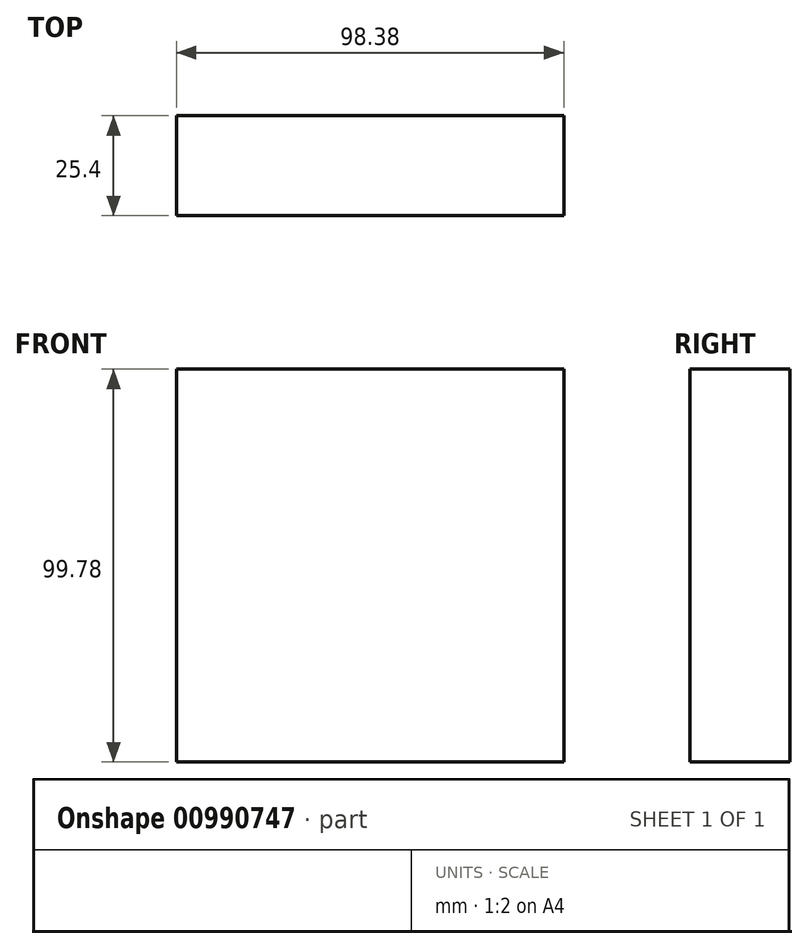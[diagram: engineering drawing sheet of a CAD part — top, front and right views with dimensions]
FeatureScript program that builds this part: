
annotation { "Feature Type Name" : "Feature", "Feature Type Description" : "" }
export const myFeature = defineFeature(function(context is Context, id is Id, definition is map)
    precondition{}
    {
        {
            var Q0;
            Q0=qCreatedBy(makeId("Front.planeOp"),FACE);
            var sketch = newSketch(context, id + "F0", { "sketchPlane" : qUnion([Q0])});
            skLineSegment(sketch, "E0.bottom", {"start": v(49.2, 49.89) * mm, "end": v(-49.2, 49.89) * mm});
            skLineSegment(sketch, "E0.top", {"start": v(49.2, -49.89) * mm, "end": v(-49.2, -49.89) * mm});
            skLineSegment(sketch, "E0.left", {"start": v(49.2, 49.89) * mm, "end": v(49.2, -49.89) * mm});
            skLineSegment(sketch, "E0.right", {"start": v(-49.2, 49.89) * mm, "end": v(-49.2, -49.89) * mm});
            skPoint(sketch, "E0.middle", {"position": v(0, 0) * mm});
            skSolve(sketch);
        }
        {
            var Q0;
            Q0=makeQuery(id+"F0.imprint","IMPRINT",FACE,{"disambiguationData":[TD([[makeQuery(id+"F0.imprint","IMPRINT",EDGE,{"derivedFrom":sQuery(id+"F0.wireOp",EDGE,"E0.bottom")}),1.0]])]});
            extrude(context, id + "F1", {"entities" : qUnion([Q0]), "depth" : 25.4 * mm, "offsetDistance" : 25.4 * mm});
        }
    });
